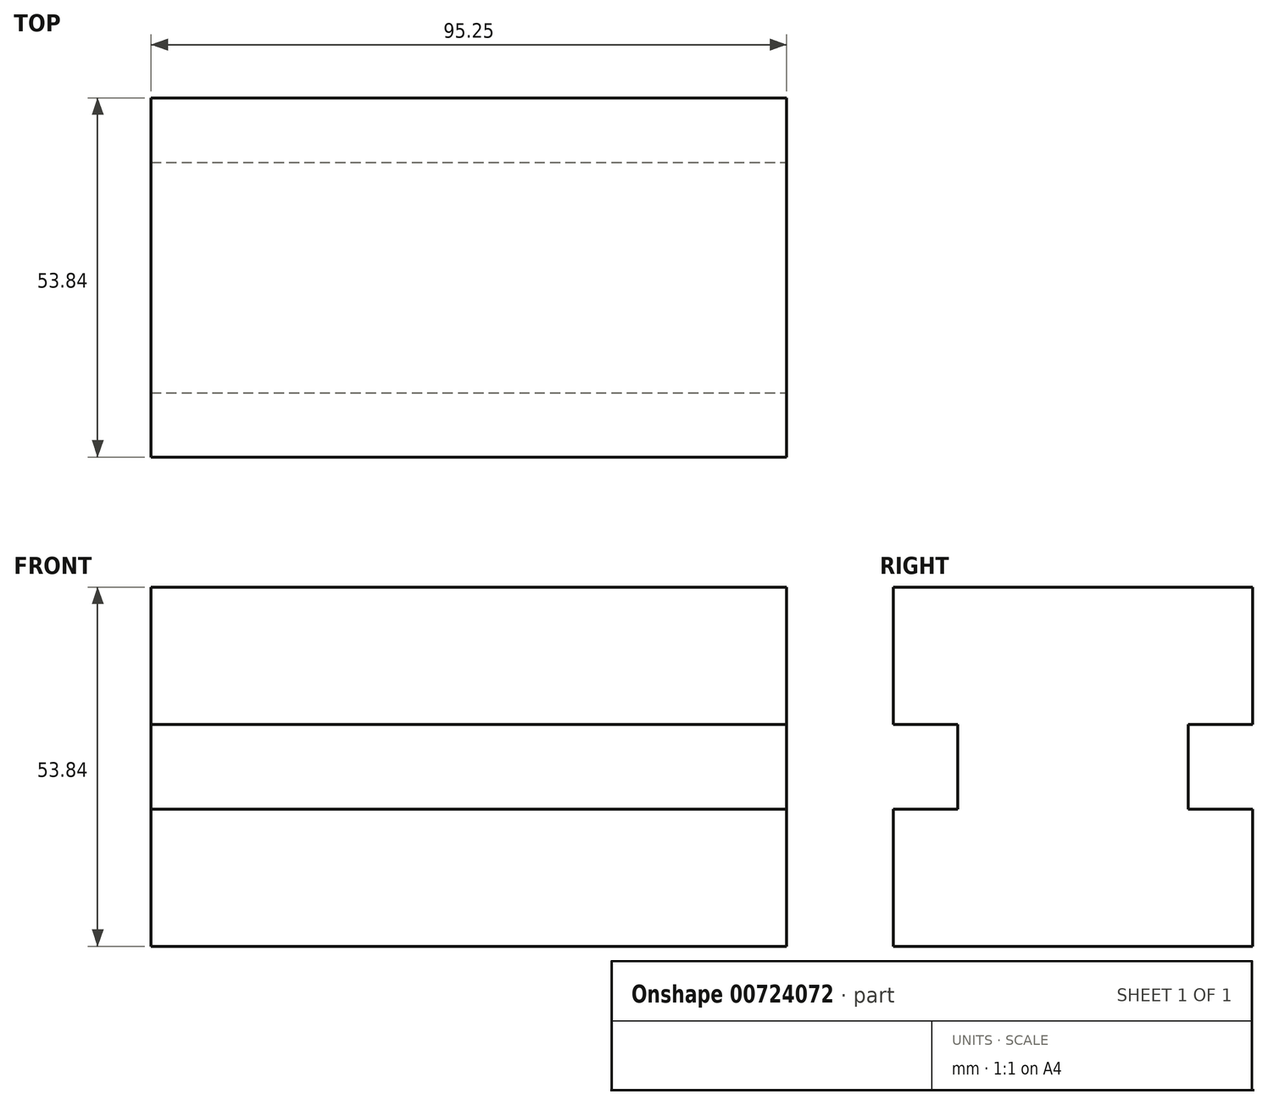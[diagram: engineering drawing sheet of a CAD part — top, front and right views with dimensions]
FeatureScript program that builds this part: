
annotation { "Feature Type Name" : "Feature", "Feature Type Description" : "" }
export const myFeature = defineFeature(function(context is Context, id is Id, definition is map)
    precondition{}
    {
        {
            var Q0;
            Q0=qCreatedBy(makeId("Right.planeOp"),FACE);
            var sketch = newSketch(context, id + "F0", { "sketchPlane" : qUnion([Q0])});
            skLineSegment(sketch, "E0.bottom", {"start": v(26.92, -26.92) * mm, "end": v(-26.92, -26.92) * mm});
            skLineSegment(sketch, "E0.top", {"start": v(26.92, 26.92) * mm, "end": v(-26.92, 26.92) * mm});
            skLineSegment(sketch, "E0.left", {"start": v(26.92, -26.92) * mm, "end": v(26.92, -6.35) * mm});
            skLineSegment(sketch, "E0.right", {"start": v(-26.92, -26.92) * mm, "end": v(-26.92, -6.35) * mm});
            skPoint(sketch, "E0.middle", {"position": v(0, 0) * mm});
            skLineSegment(sketch, "E1.bottom", {"start": v(-26.92, 6.35) * mm, "end": v(-17.27, 6.35) * mm});
            skLineSegment(sketch, "E1.top", {"start": v(-26.92, -6.35) * mm, "end": v(-17.27, -6.35) * mm});
            skLineSegment(sketch, "E1.right", {"start": v(-17.27, 6.35) * mm, "end": v(-17.27, -6.35) * mm});
            skLineSegment(sketch, "E2.trimOffspring", {"start": v(-26.92, 6.35) * mm, "end": v(-26.92, 26.92) * mm});
            skLineSegment(sketch, "E3", {"start": v(0, 29.65) * mm, "end": v(0, -29.89) * mm, "construction": true});
            skLineSegment(sketch, "E4.MirrorCS", {"start": v(26.92, 6.35) * mm, "end": v(17.27, 6.35) * mm});
            skLineSegment(sketch, "E5.MirrorCS", {"start": v(17.27, 6.35) * mm, "end": v(17.27, -6.35) * mm});
            skLineSegment(sketch, "E6.MirrorCS", {"start": v(26.92, -6.35) * mm, "end": v(17.27, -6.35) * mm});
            skLineSegment(sketch, "E7.trimOffspring", {"start": v(26.92, 6.35) * mm, "end": v(26.92, 26.92) * mm});
            skSolve(sketch);
        }
        {
            var Q0;
            Q0=makeQuery(id+"F0.imprint","IMPRINT",FACE,{"disambiguationData":[TD([[makeQuery(id+"F0.imprint","IMPRINT",EDGE,{"derivedFrom":sQuery(id+"F0.wireOp",EDGE,"E0.bottom")}),-1.0]])]});
            extrude(context, id + "F1", {"entities" : qUnion([Q0]), "oppositeDirection" : true, "depth" : 95.25 * mm, "offsetDistance" : 25.4 * mm});
        }
    });
